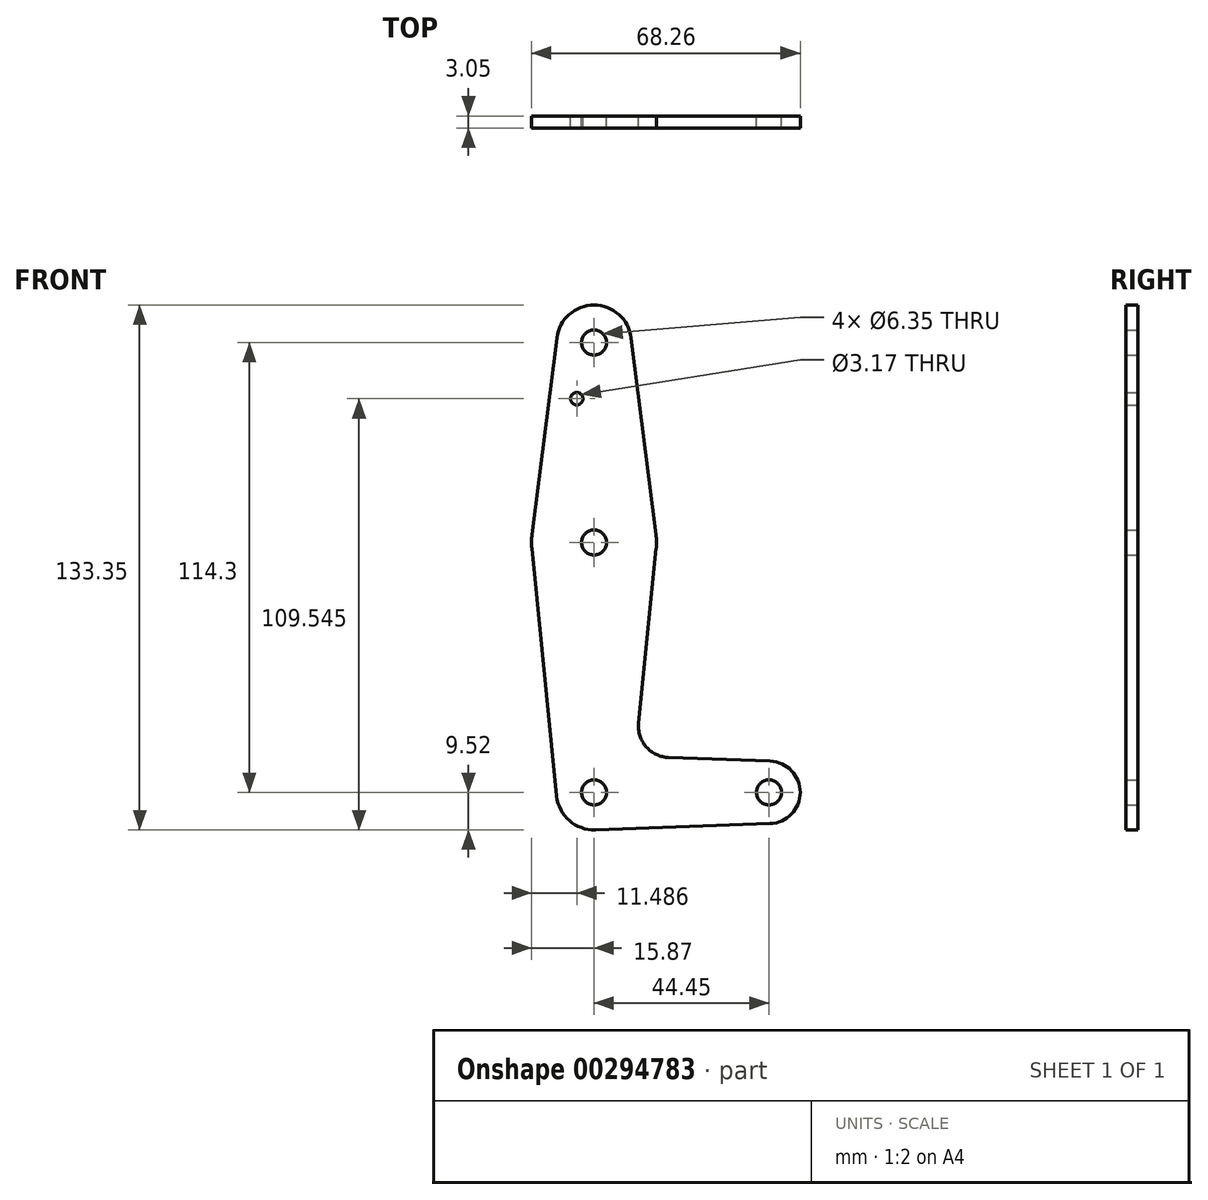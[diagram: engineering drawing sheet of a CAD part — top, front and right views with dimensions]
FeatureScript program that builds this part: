
annotation { "Feature Type Name" : "Feature", "Feature Type Description" : "" }
export const myFeature = defineFeature(function(context is Context, id is Id, definition is map)
    precondition{}
    {
        {
            var Q0;
            Q0=qCreatedBy(makeId("Front.planeOp"),FACE);
            var sketch = newSketch(context, id + "F0", { "sketchPlane" : qUnion([Q0])});
            skCircle(sketch, "E0", {"center": v(0, 0) * mm, "radius": 9.53 * mm});
            skCircle(sketch, "E1", {"center": v(0, 63.5) * mm, "radius": 15.88 * mm});
            skCircle(sketch, "E2", {"center": v(0, 114.3) * mm, "radius": 9.53 * mm});
            skCircle(sketch, "E3", {"center": v(44.45, 0) * mm, "radius": 7.94 * mm});
            skLineSegment(sketch, "E4", {"start": v(0, 0) * mm, "end": v(44.45, 0) * mm, "construction": true});
            skLineSegment(sketch, "E5", {"start": v(0, 0) * mm, "end": v(0, 63.5) * mm, "construction": true});
            skLineSegment(sketch, "E6", {"start": v(0, 63.5) * mm, "end": v(0, 114.3) * mm, "construction": true});
            skLineSegment(sketch, "E7", {"start": v(-9.45, 115.5) * mm, "end": v(-15.75, 65.48) * mm});
            skLineSegment(sketch, "E8", {"start": v(15.8, 61.91) * mm, "end": v(11.34, 17.6) * mm});
            skPoint(sketch, "E9.startSnap0", {"position": v(0, 31.75) * mm});
            skLineSegment(sketch, "E10", {"start": v(9.45, 115.5) * mm, "end": v(15.75, 65.48) * mm});
            skLineSegment(sketch, "E11", {"start": v(-15.8, 61.91) * mm, "end": v(-9.48, -0.95) * mm});
            skLineSegment(sketch, "E12", {"start": v(0.34, -9.52) * mm, "end": v(44.73, -7.93) * mm});
            skLineSegment(sketch, "E13", {"start": v(18.97, 8.85) * mm, "end": v(44.73, 7.93) * mm});
            skPoint(sketch, "E14.newPointA", {"position": v(0.34, 9.52) * mm});
            skPoint(sketch, "E14.newPointB", {"position": v(9.48, -0.95) * mm});
            skArc(sketch, "E14.filletArc", {"start": v(11.34, 17.6) * mm, "mid": v(13.26, 11.57) * mm, "end": v(18.97, 8.85) * mm});
            skCircle(sketch, "E15", {"center": v(-4.38, 100.03) * mm, "radius": 1.59 * mm});
            skCircle(sketch, "E16", {"center": v(0, 114.3) * mm, "radius": 3.18 * mm});
            skCircle(sketch, "E17", {"center": v(0, 63.5) * mm, "radius": 3.18 * mm});
            skCircle(sketch, "E18", {"center": v(0, 0) * mm, "radius": 3.18 * mm});
            skCircle(sketch, "E19", {"center": v(44.45, 0) * mm, "radius": 3.18 * mm});
            skSolve(sketch);
        }
        {
            var Q0;
            Q0=makeQuery(id+"F0.imprint","IMPRINT",FACE,{"disambiguationData":[TD([[makeQuery(id+"F0.imprint","IMPRINT",EDGE,{"derivedFrom":sQuery(id+"F0.wireOp",EDGE,"E16")}),-1.0]])]});
            var Q1;
            {var subQ0=sQuery(id+"F0.wireOp",EDGE,"E7");Q1=makeQuery(id+"F0.imprint","IMPRINT",FACE,{"disambiguationData":[TD([[makeQuery(id+"F0.imprint","IMPRINT",EDGE,{"derivedFrom":subQ0}),1.0]])]});}
            var Q2;
            Q2=makeQuery(id+"F0.imprint","IMPRINT",FACE,{"disambiguationData":[TD([[makeQuery(id+"F0.imprint","IMPRINT",EDGE,{"derivedFrom":sQuery(id+"F0.wireOp",EDGE,"E17")}),-1.0]])]});
            var Q3;
            {var subQ3=sQuery(id+"F0.wireOp",EDGE,"E8");Q3=makeQuery(id+"F0.imprint","IMPRINT",FACE,{"disambiguationData":[TD([[makeQuery(id+"F0.imprint","IMPRINT",EDGE,{"derivedFrom":subQ3}),-1.0]])]});}
            var Q4;
            Q4=makeQuery(id+"F0.imprint","IMPRINT",FACE,{"disambiguationData":[TD([[makeQuery(id+"F0.imprint","IMPRINT",EDGE,{"derivedFrom":sQuery(id+"F0.wireOp",EDGE,"E18")}),-1.0]])]});
            var Q5;
            Q5=makeQuery(id+"F0.imprint","IMPRINT",FACE,{"disambiguationData":[TD([[makeQuery(id+"F0.imprint","IMPRINT",EDGE,{"derivedFrom":sQuery(id+"F0.wireOp",EDGE,"E19")}),-1.0]])]});
            extrude(context, id + "F1", {"entities" : qUnion([Q0, Q1, Q2, Q3, Q4, Q5]), "depth" : 3.05 * mm});
        }
    });
